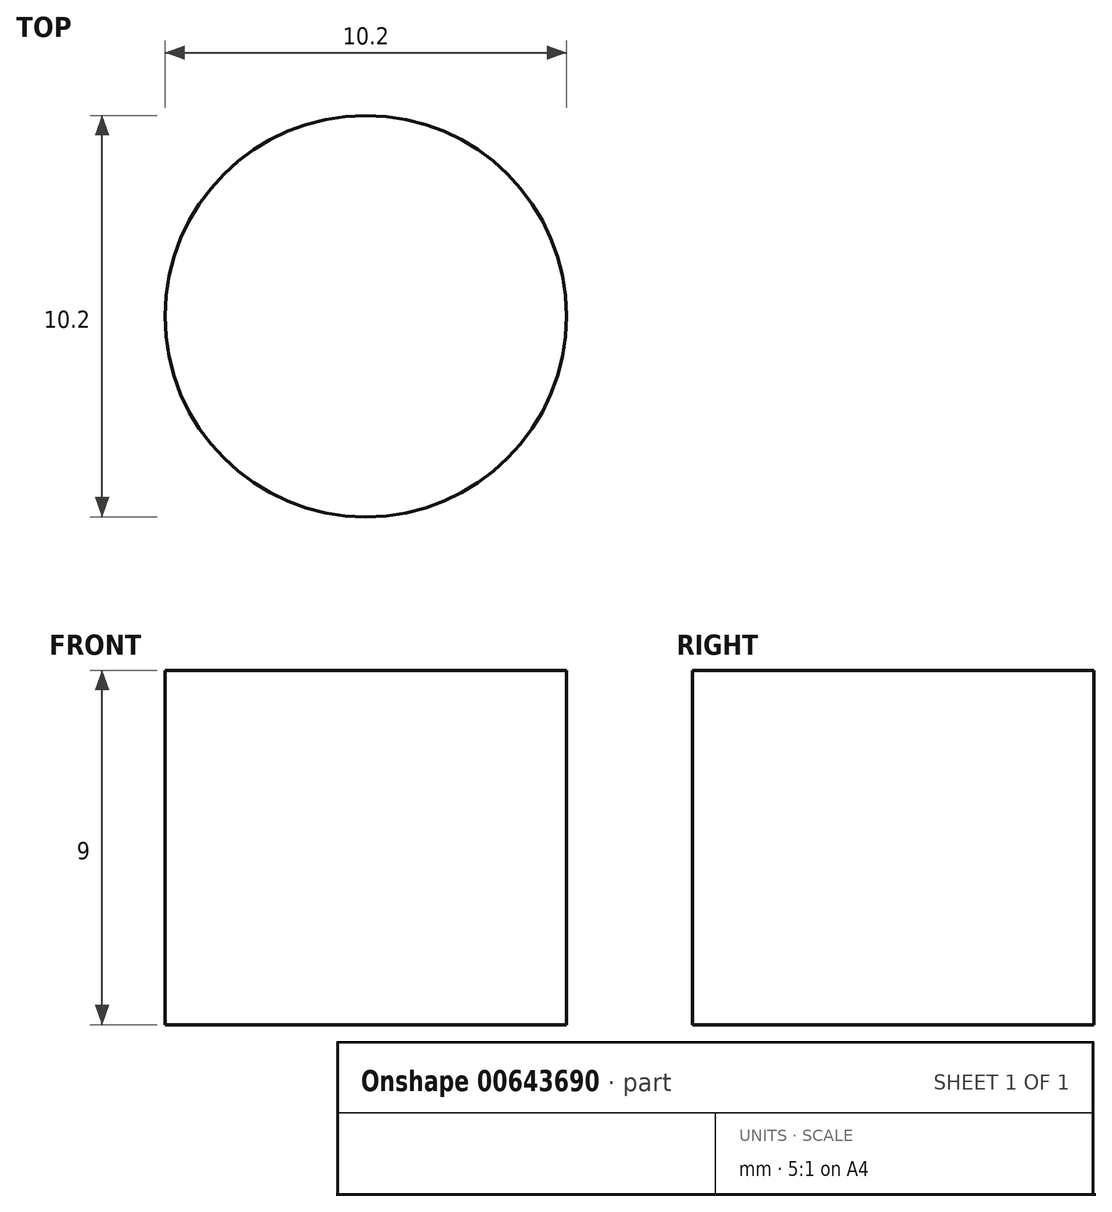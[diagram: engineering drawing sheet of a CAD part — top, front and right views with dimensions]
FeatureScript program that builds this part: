
annotation { "Feature Type Name" : "Feature", "Feature Type Description" : "" }
export const myFeature = defineFeature(function(context is Context, id is Id, definition is map)
    precondition{}
    {
        {
            var Q0;
            Q0=qCreatedBy(makeId("Top.planeOp"),FACE);
            var sketch = newSketch(context, id + "F0", { "sketchPlane" : qUnion([Q0])});
            skCircle(sketch, "E0", {"center": v(0, 0) * mm, "radius": 5.1 * mm});
            skSolve(sketch);
        }
        {
            var Q0;
            Q0 = qSketchRegion(id + "F0", true);
            extrude(context, id + "F1", {"entities" : qUnion([Q0]), "depth" : 9 * mm, "offsetDistance" : 25 * mm});
        }
    });
